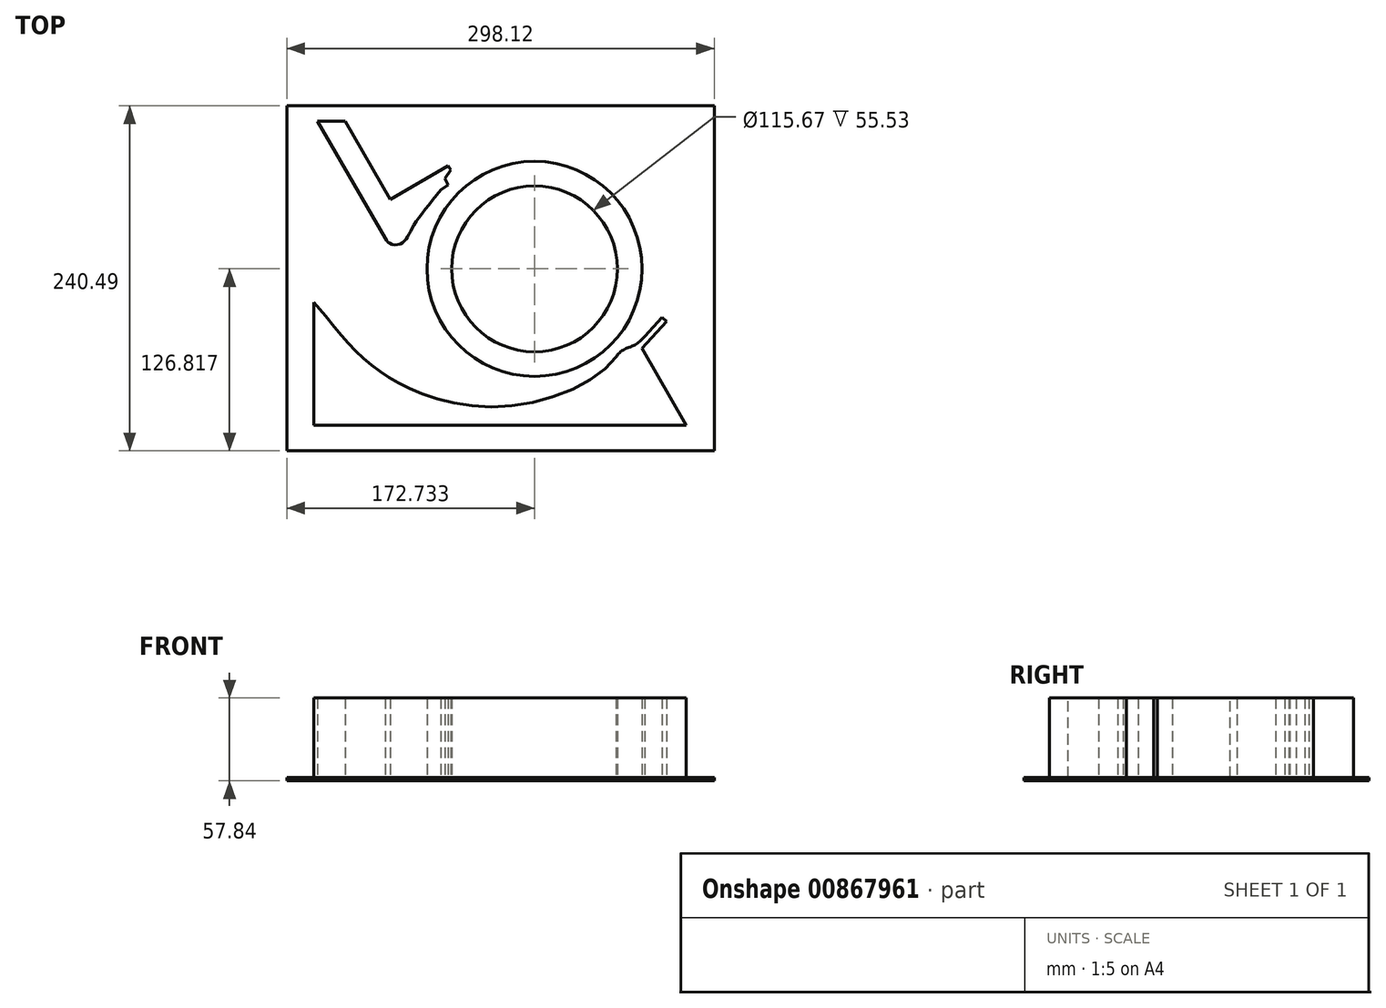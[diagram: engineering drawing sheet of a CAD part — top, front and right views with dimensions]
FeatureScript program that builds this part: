
annotation { "Feature Type Name" : "Feature", "Feature Type Description" : "" }
export const myFeature = defineFeature(function(context is Context, id is Id, definition is map)
    precondition{}
    {
        {
            var Q0;
            Q0=qCreatedBy(makeId("Top.planeOp"),FACE);
            var sketch = newSketch(context, id + "F0", { "sketchPlane" : qUnion([Q0])});
            skCircle(sketch, "E0", {"center": v(24.5, -2.25) * mm, "radius": 25 * mm});
            skCircle(sketch, "E1", {"center": v(24.5, -2.25) * mm, "radius": 32.41 * mm});
            skLineSegment(sketch, "E2", {"start": v(-18.97, 18.73) * mm, "end": v(-1.53, 28.84) * mm});
            skLineSegment(sketch, "E3", {"start": v(-18.97, 18.73) * mm, "end": v(-32.62, 42.3) * mm});
            skLineSegment(sketch, "E4", {"start": v(-32.62, 42.3) * mm, "end": v(-40.92, 42.3) * mm});
            skLineSegment(sketch, "E5", {"start": v(-40.92, 42.3) * mm, "end": v(-20.5, 7.05) * mm});
            skLineSegment(sketch, "E6", {"start": v(-41.99, -12.35) * mm, "end": v(-41.99, -49.41) * mm});
            skLineSegment(sketch, "E7", {"start": v(-41.99, -49.41) * mm, "end": v(70.23, -49.41) * mm});
            skLineSegment(sketch, "E8", {"start": v(70.23, -49.41) * mm, "end": v(56.84, -26.27) * mm});
            skLineSegment(sketch, "E9", {"start": v(56.84, -26.27) * mm, "end": v(64.3, -18.04) * mm});
            skLineSegment(sketch, "E10", {"start": v(64.3, -18.04) * mm, "end": v(63, -16.86) * mm});
            skPoint(sketch, "E11.0", {"position": v(-41.99, -49.41) * mm});
            skLineSegment(sketch, "E12", {"start": v(63, -16.86) * mm, "end": v(57.76, -22.64) * mm});
            skFitSpline(sketch, "E13", {"points": [v(57.76, -22.64) * mm, v(54.63, -25.22) * mm, v(51.24, -26.68) * mm, v(49.1, -28.78) * mm], "startDerivative": vector(-9.59, -9.6) * mm, "endDerivative": vector(-3.86, -6.82) * mm});
            skFitSpline(sketch, "E14", {"points": [v(-41.99, -12.35) * mm, v(-31.03, -25.29) * mm, v(-23, -32.5) * mm, v(-12.25, -38.75) * mm, v(16.67, -43.63) * mm, v(49.1, -28.78) * mm], "startDerivative": vector(90.88, -105.67) * mm, "endDerivative": vector(62.26, 87.02) * mm});
            skLineSegment(sketch, "E15", {"start": v(-0.76, 27.6) * mm, "end": v(-1.53, 28.84) * mm});
            skLineSegment(sketch, "E16", {"start": v(-0.76, 27.6) * mm, "end": v(-2.5, 24.95) * mm});
            skLineSegment(sketch, "E17", {"start": v(-2.5, 24.95) * mm, "end": v(-1.5, 23) * mm});
            skLineSegment(sketch, "E18", {"start": v(-1.5, 23) * mm, "end": v(-3.73, 21.54) * mm});
            skFitSpline(sketch, "E19", {"points": [v(-3.73, 21.54) * mm, v(-10.9, 12.45) * mm, v(-13.3, 8.25) * mm, v(-14.84, 6.06) * mm, v(-17, 5.01) * mm, v(-19.26, 5.53) * mm, v(-20.5, 7.05) * mm], "startDerivative": vector(-28.62, -36.37) * mm, "endDerivative": vector(-12.48, 18.42) * mm});
            skLineSegment(sketch, "E20.bottom", {"start": v(-50.16, 46.87) * mm, "end": v(78.68, 46.87) * mm});
            skLineSegment(sketch, "E20.top", {"start": v(-50.16, -57.06) * mm, "end": v(78.68, -57.06) * mm});
            skLineSegment(sketch, "E20.left", {"start": v(-50.16, 46.87) * mm, "end": v(-50.16, -57.06) * mm});
            skLineSegment(sketch, "E20.right", {"start": v(78.68, 46.87) * mm, "end": v(78.68, -57.06) * mm});
            skSolve(sketch);
        }
        {
            var Q0;
            Q0 = qSketchRegion(id + "F0", true);
            var Q1;
            Q1=makeQuery(id+"F0.imprint","IMPRINT",FACE,{"disambiguationData":[TD([[makeQuery(id+"F0.imprint","IMPRINT",EDGE,{"derivedFrom":sQuery(id+"F0.wireOp",EDGE,"E0")}),-1.0]])]});
            var Q2;
            Q2=makeQuery(id+"F0.imprint","IMPRINT",FACE,{"disambiguationData":[TD([[makeQuery(id+"F0.imprint","IMPRINT",EDGE,{"derivedFrom":sQuery(id+"F0.wireOp",EDGE,"E0")}),1.0]])]});
            var Q3;
            Q3=makeQuery(id+"F0.imprint","IMPRINT",FACE,{"disambiguationData":[TD([[makeQuery(id+"F0.imprint","IMPRINT",EDGE,{"derivedFrom":sQuery(id+"F0.wireOp",EDGE,"E2")}),-1.0]])]});
            var Q4;
            Q4=makeQuery(id+"F0.imprint","IMPRINT",FACE,{"disambiguationData":[TD([[makeQuery(id+"F0.imprint","IMPRINT",EDGE,{"derivedFrom":sQuery(id+"F0.wireOp",EDGE,"E6")}),1.0]])]});
            extrude(context, id + "F1", {"entities" : qUnion([Q0, Q1, Q2, Q3, Q4]), "depth" : 1 * mm, "offsetDistance" : 25 * mm});
        }
        {
            var Q0;
            Q0=makeQuery(id+"F0.imprint","IMPRINT",FACE,{"disambiguationData":[TD([[makeQuery(id+"F0.imprint","IMPRINT",EDGE,{"derivedFrom":sQuery(id+"F0.wireOp",EDGE,"E2")}),-1.0]])]});
            var Q1;
            Q1=makeQuery(id+"F0.imprint","IMPRINT",FACE,{"disambiguationData":[TD([[makeQuery(id+"F0.imprint","IMPRINT",EDGE,{"derivedFrom":sQuery(id+"F0.wireOp",EDGE,"E0")}),-1.0]])]});
            var Q2;
            Q2=makeQuery(id+"F0.imprint","IMPRINT",FACE,{"disambiguationData":[TD([[makeQuery(id+"F0.imprint","IMPRINT",EDGE,{"derivedFrom":sQuery(id+"F0.wireOp",EDGE,"E6")}),1.0]])]});
            extrude(context, id + "F2", {"entities" : qUnion([Q0, Q1, Q2]), "operationType" : NewBodyOperationType.ADD, "depth" : 25 * mm, "offsetDistance" : 25 * mm});
        }
        {
            var Q0;
            Q0=makeQuery(id+"F1.opExtrude","SWEPT_BODY",BODY,{"disambiguationData":[OSD([sQuery(id+"F0.wireOp",EDGE,"E20.bottom"),sQuery(id+"F0.wireOp",EDGE,"E20.top"),sQuery(id+"F0.wireOp",EDGE,"E20.left"),sQuery(id+"F0.wireOp",EDGE,"E20.right")])]});
            var Q1;
            Q1=sQuery(id+"F0.wireOp",VERTEX,"E0.center");
            transform(context, id + "F3", {"entities" : qUnion([Q0]), "transformType" : TransformType.SCALE_UNIFORMLY, "scale" : 2.31, "scalePoint" : qUnion([Q1]), "makeCopy" : false});
        }
    });
